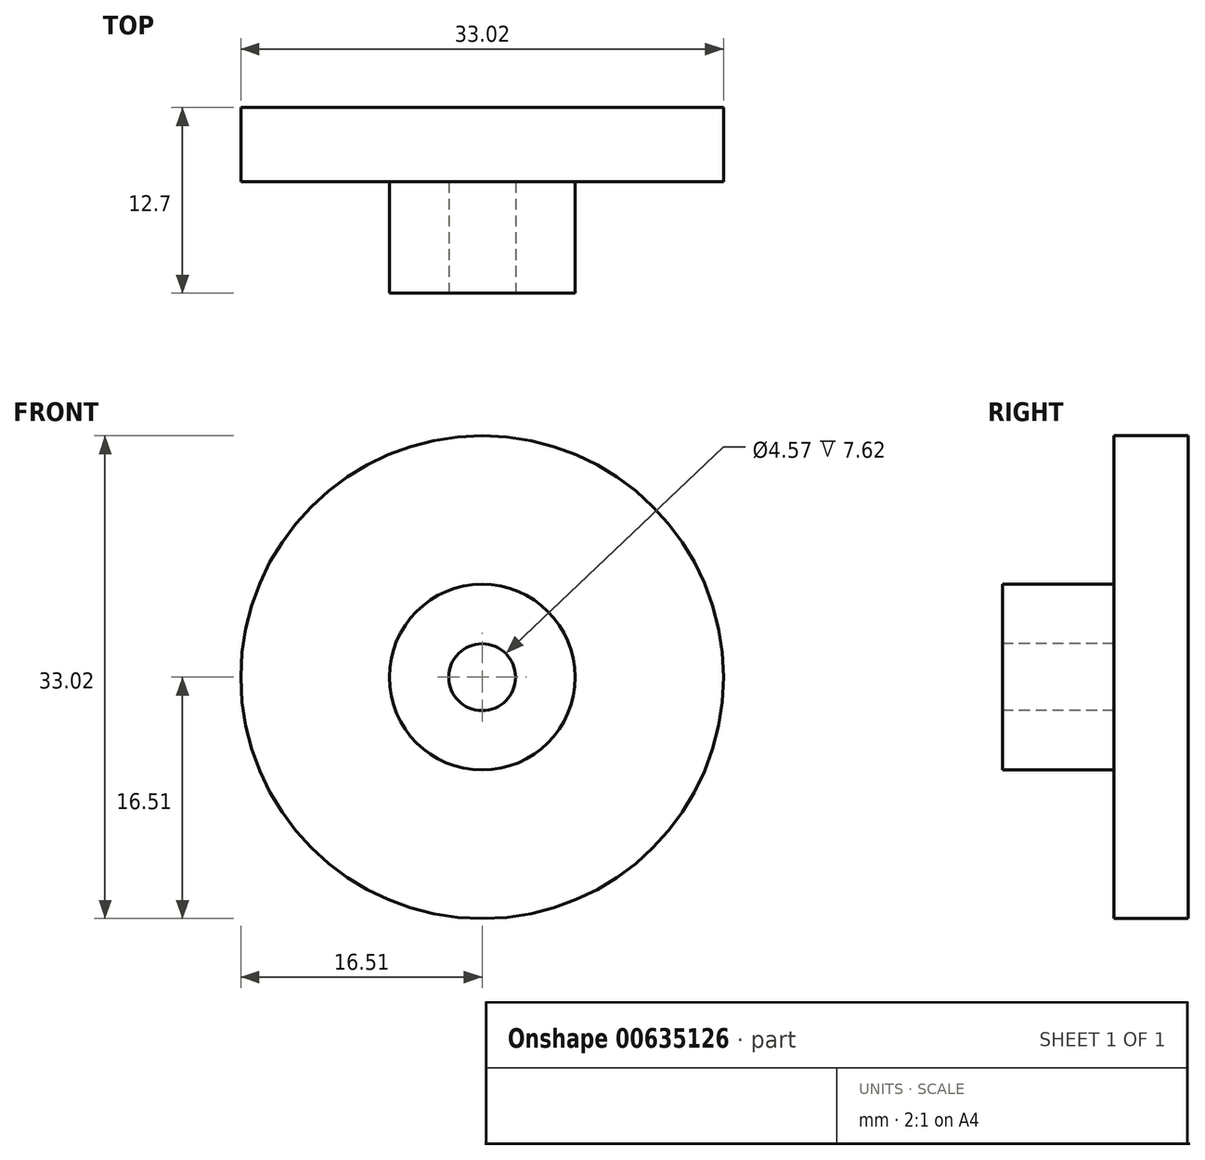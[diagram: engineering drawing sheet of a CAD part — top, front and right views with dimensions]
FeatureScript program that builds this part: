
annotation { "Feature Type Name" : "Feature", "Feature Type Description" : "" }
export const myFeature = defineFeature(function(context is Context, id is Id, definition is map)
    precondition{}
    {
        {
            var Q0;
            Q0=qCreatedBy(makeId("Front.planeOp"),FACE);
            var sketch = newSketch(context, id + "F0", { "sketchPlane" : qUnion([Q0])});
            skCircle(sketch, "E0", {"center": v(0, 0) * mm, "radius": 16.51 * mm});
            skSolve(sketch);
        }
        {
            var Q0;
            Q0=makeQuery(id+"F0.imprint","IMPRINT",FACE,{"disambiguationData":[TD([[makeQuery(id+"F0.imprint","IMPRINT",EDGE,{"derivedFrom":sQuery(id+"F0.wireOp",EDGE,"E0")}),1.0]])]});
            extrude(context, id + "F1", {"entities" : qUnion([Q0]), "oppositeDirection" : true, "depth" : 12.7 * mm, "offsetDistance" : 25.4 * mm});
        }
        {
            var Q0;
            Q0=makeQuery(id+"F1.opExtrude","CAP_FACE",FACE,{"disambiguationData":[OSD([sQuery(id+"F0.wireOp",EDGE,"E0")])],"isStart":true});
            var sketch = newSketch(context, id + "F2", { "sketchPlane" : qUnion([Q0])});
            skCircle(sketch, "E1", {"center": v(0, 0) * mm, "radius": 2.29 * mm});
            skSolve(sketch);
        }
        {
            var Q0;
            Q0=makeQuery(id+"F2.imprint","IMPRINT",FACE,{"disambiguationData":[TD([[makeQuery(id+"F2.imprint","IMPRINT",EDGE,{"derivedFrom":sQuery(id+"F2.wireOp",EDGE,"E1")}),1.0]])]});
            extrude(context, id + "F3", {"entities" : qUnion([Q0]), "operationType" : NewBodyOperationType.REMOVE, "oppositeDirection" : true, "depth" : 7.62 * mm, "offsetDistance" : 25.4 * mm});
        }
        {
            var Q0;
            Q0=makeQuery(id+"F1.opExtrude","CAP_FACE",FACE,{"disambiguationData":[OSD([sQuery(id+"F0.wireOp",EDGE,"E0")])],"isStart":true});
            var sketch = newSketch(context, id + "F4", { "sketchPlane" : qUnion([Q0])});
            skCircle(sketch, "E2", {"center": v(0, 0) * mm, "radius": 6.35 * mm});
            skSolve(sketch);
        }
        {
            var Q0;
            Q0=makeQuery(id+"F4.imprint","IMPRINT",FACE,{"disambiguationData":[TD([[makeQuery(id+"F4.imprint","IMPRINT",EDGE,{"derivedFrom":sQuery(id+"F4.wireOp",EDGE,"E2")}),-1.0]])]});
            extrude(context, id + "F5", {"entities" : qUnion([Q0]), "operationType" : NewBodyOperationType.REMOVE, "oppositeDirection" : true, "depth" : 7.62 * mm, "offsetDistance" : 25.4 * mm});
        }
    });
